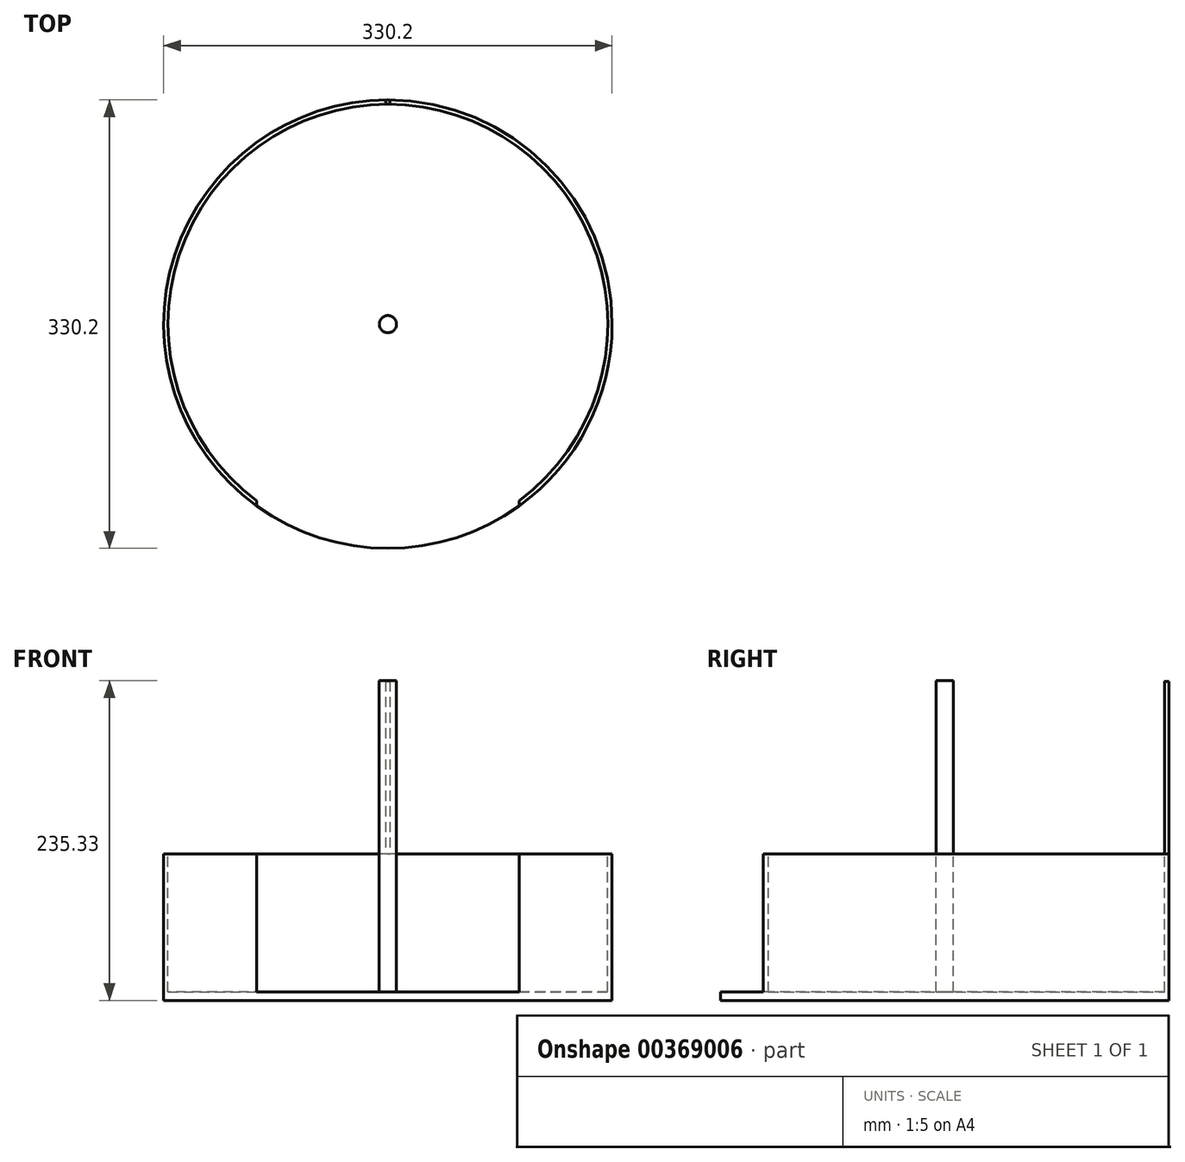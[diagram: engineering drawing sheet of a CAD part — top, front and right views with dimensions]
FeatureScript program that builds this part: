
annotation { "Feature Type Name" : "Feature", "Feature Type Description" : "" }
export const myFeature = defineFeature(function(context is Context, id is Id, definition is map)
    precondition{}
    {
        {
            var Q0;
            Q0=qCreatedBy(makeId("Front.planeOp"),FACE);
            var sketch = newSketch(context, id + "F0", { "sketchPlane" : qUnion([Q0])});
            skLineSegment(sketch, "E0", {"start": v(0, 0) * mm, "end": v(0, 70.61) * mm});
            skLineSegment(sketch, "E1", {"start": v(0, 70.61) * mm, "end": v(0, -59.58) * mm});
            skSolve(sketch);
        }
        {
            var Q0;
            Q0=qCreatedBy(makeId("Front.planeOp"),FACE);
            var sketch = newSketch(context, id + "F1", { "sketchPlane" : qUnion([Q0])});
            skLineSegment(sketch, "E2.top", {"start": v(-165.1, 101.22) * mm, "end": v(-161.93, 101.22) * mm});
            skLineSegment(sketch, "E2.left", {"start": v(-165.1, -0.38) * mm, "end": v(-165.1, 101.22) * mm});
            skLineSegment(sketch, "E2.right", {"start": v(-161.92, -0.39) * mm, "end": v(-161.93, 101.22) * mm});
            skLineSegment(sketch, "E3.top", {"start": v(0, 228.6) * mm, "end": v(-6.35, 228.6) * mm});
            skLineSegment(sketch, "E3.left", {"start": v(0, 0) * mm, "end": v(0, 228.6) * mm});
            skLineSegment(sketch, "E3.right", {"start": v(-6.35, -0.39) * mm, "end": v(-6.35, 228.6) * mm});
            skLineSegment(sketch, "E4", {"start": v(-161.92, -0.39) * mm, "end": v(-6.35, -0.39) * mm});
            skLineSegment(sketch, "E5", {"start": v(0, 0) * mm, "end": v(0, -6.73) * mm});
            skLineSegment(sketch, "E6", {"start": v(0, -6.73) * mm, "end": v(-165.1, -6.73) * mm});
            skLineSegment(sketch, "E7", {"start": v(-165.1, -6.73) * mm, "end": v(-165.1, -0.38) * mm});
            skSolve(sketch);
        }
        {
            var Q0;
            Q0 = qSketchRegion(id + "F1", true);
            var Q1;
            Q1=sQuery(id+"F0.wireOp",EDGE,"E1");
            revolve(context, id + "F2", {"entities" : qUnion([Q0]), "axis" : qUnion([Q1]), "revolveType" : RevolveType.FULL});
        }
        {
            var Q0;
            Q0=makeQuery(id+"F2.opRevolve","SWEPT_FACE",FACE,{"disambiguationData":[OSD([sQuery(id+"F1.wireOp",EDGE,"E2.top")])]});
            var sketch = newSketch(context, id + "F3", { "sketchPlane" : qUnion([Q0])});
            skArc(sketch, "E8", {"start": v(-96.6, -129.95) * mm, "mid": v(0, -161.93) * mm, "end": v(96.6, -129.95) * mm});
            skArc(sketch, "E9", {"start": v(-96.6, -133.89) * mm, "mid": v(0, -165.1) * mm, "end": v(96.6, -133.89) * mm});
            skLineSegment(sketch, "E10", {"start": v(-96.6, -129.95) * mm, "end": v(-96.6, -133.89) * mm});
            skLineSegment(sketch, "E11", {"start": v(96.6, -129.95) * mm, "end": v(96.6, -133.89) * mm});
            skSolve(sketch);
        }
        {
            var Q0;
            Q0 = qSketchRegion(id + "F3", true);
            var Q1;
            Q1=makeQuery(id+"F2.opRevolve","SWEPT_FACE",FACE,{"disambiguationData":[OSD([sQuery(id+"F1.wireOp",EDGE,"E4")])]});
            extrude(context, id + "F4", {"entities" : qUnion([Q0]), "operationType" : NewBodyOperationType.REMOVE, "endBound" : BoundingType.UP_TO_SURFACE, "oppositeDirection" : true, "endBoundEntityFace" : qUnion([Q1]), "depth" : 38.1 * mm});
        }
        {
            var Q0;
            Q0=makeQuery(id+"F2.opRevolve","SWEPT_FACE",FACE,{"disambiguationData":[OSD([sQuery(id+"F1.wireOp",EDGE,"E2.top")])]});
            var sketch = newSketch(context, id + "F5", { "sketchPlane" : qUnion([Q0])});
            skCircle(sketch, "E12", {"center": v(0, 163.51) * mm, "radius": 1.59 * mm});
            skPoint(sketch, "E12.centerSnap0", {"position": v(0, 161.92) * mm});
            skSolve(sketch);
        }
        {
            var Q0;
            Q0 = qSketchRegion(id + "F5", true);
            extrude(context, id + "F6", {"entities" : qUnion([Q0]), "operationType" : NewBodyOperationType.ADD, "depth" : 127 * mm});
        }
    });
